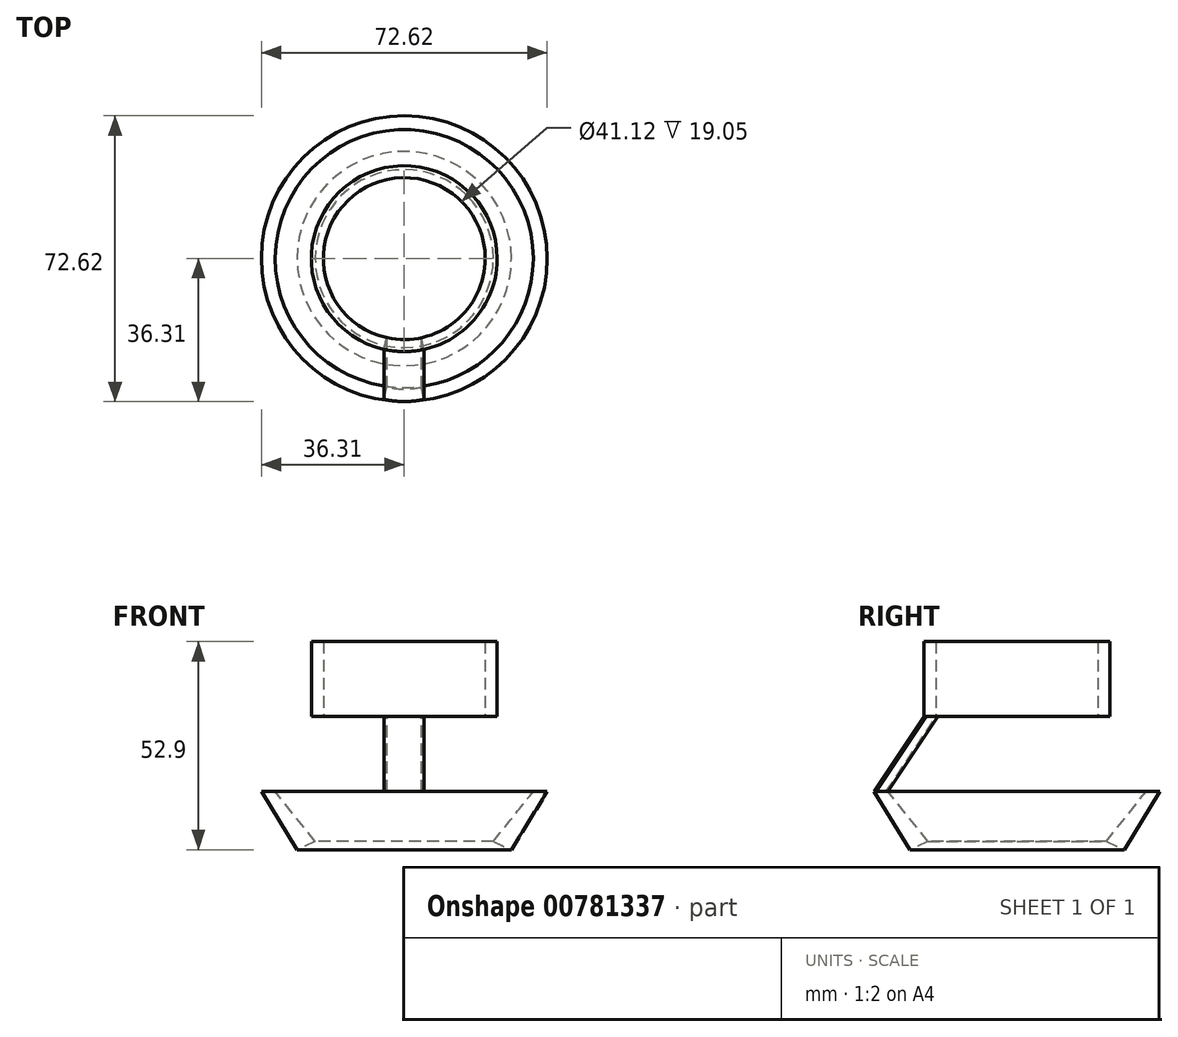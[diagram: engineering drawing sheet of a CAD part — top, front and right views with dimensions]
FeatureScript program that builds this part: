
annotation { "Feature Type Name" : "Feature", "Feature Type Description" : "" }
export const myFeature = defineFeature(function(context is Context, id is Id, definition is map)
    precondition{}
    {
        {
            var Q0;
            Q0=qCreatedBy(makeId("Top.planeOp"),FACE);
            var sketch = newSketch(context, id + "F0", { "sketchPlane" : qUnion([Q0])});
            skCircle(sketch, "E0", {"center": v(0, 0) * mm, "radius": 20.56 * mm});
            skCircle(sketch, "E1.0", {"center": v(0, 0) * mm, "radius": 23.6 * mm});
            skSolve(sketch);
        }
        {
            var Q0;
            Q0 = qSketchRegion(id + "F0", true);
            extrude(context, id + "F1", {"entities" : qUnion([Q0]), "depth" : 19.05 * mm, "offsetDistance" : 25.4 * mm});
        }
        {
            var Q0;
            Q0=makeQuery(id+"F1.opExtrude","CAP_FACE",FACE,{"disambiguationData":[OSD([sQuery(id+"F0.wireOp",EDGE,"E0"),sQuery(id+"F0.wireOp",EDGE,"E1.0")])],"isStart":true});
            var sketch = newSketch(context, id + "F2", { "sketchPlane" : qUnion([Q0])});
            skLineSegment(sketch, "E2", {"start": v(0, 0) * mm, "end": v(0, 22.55) * mm, "construction": true});
            skLineSegment(sketch, "E3", {"start": v(0, 22.55) * mm, "end": v(5.08, 22.55) * mm, "construction": true});
            skLineSegment(sketch, "E4", {"start": v(0, 22.55) * mm, "end": v(-5.08, 22.55) * mm, "construction": true});
            skLineSegment(sketch, "E5", {"start": v(-5.08, 22.55) * mm, "end": v(-5.08, 19.92) * mm, "construction": true});
            skLineSegment(sketch, "E6", {"start": v(5.08, 22.55) * mm, "end": v(5.08, 19.92) * mm, "construction": true});
            skLineSegment(sketch, "E7", {"start": v(-5.08, 23.06) * mm, "end": v(-4.42, 20.08) * mm});
            skLineSegment(sketch, "E8", {"start": v(5.08, 23.06) * mm, "end": v(4.42, 20.08) * mm});
            skArc(sketch, "E9.0", {"start": v(5.08, 23.06) * mm, "mid": v(0, 23.6) * mm, "end": v(-5.08, 23.06) * mm});
            skArc(sketch, "E10.0", {"start": v(5.08, 19.92) * mm, "mid": v(0, 20.56) * mm, "end": v(-5.08, 19.92) * mm});
            skPoint(sketch, "E11", {"position": v(-19.8, 0) * mm});
            skPoint(sketch, "E12", {"position": v(0, 23.6) * mm});
            skSolve(sketch);
        }
        {
            var Q0;
            Q0=qCreatedBy(makeId("Right.planeOp"),FACE);
            var sketch = newSketch(context, id + "F3", { "sketchPlane" : qUnion([Q0])});
            skPoint(sketch, "E13.0", {"position": v(-23.6, 0) * mm});
            skLineSegment(sketch, "E14", {"start": v(-23.6, 0) * mm, "end": v(-36.3, 0) * mm, "construction": true});
            skLineSegment(sketch, "E15", {"start": v(-36.3, 0) * mm, "end": v(-36.3, -19.05) * mm, "construction": true});
            skLineSegment(sketch, "E16", {"start": v(-36.3, -19.05) * mm, "end": v(-23.6, 0) * mm});
            skSolve(sketch);
        }
        {
            var Q0;
            {var subQ0=sQuery(id+"F2.wireOp",EDGE,"E7");Q0=makeQuery(id+"F2.imprint","IMPRINT",FACE,{"disambiguationData":[TD([[makeQuery(id+"F2.imprint","IMPRINT",EDGE,{"derivedFrom":subQ0}),1.0]])]});}
            var Q1;
            Q1=sQuery(id+"F3.wireOp",EDGE,"E16");
            sweep(context, id + "F4", {"operationType" : NewBodyOperationType.ADD, "profiles" : qUnion([Q0]), "path" : qUnion([Q1])});
        }
        {
            var Q0;
            Q0=qCreatedBy(makeId("Right.planeOp"),FACE);
            var sketch = newSketch(context, id + "F5", { "sketchPlane" : qUnion([Q0])});
            skLineSegment(sketch, "E17", {"start": v(0, -13.55) * mm, "end": v(0, 29.8) * mm});
            skSolve(sketch);
        }
        {
            var Q0;
            Q0=makeQuery(id+"F4.opSweep","CAP_FACE",FACE,{"disambiguationData":[OSD([sQuery(id+"F2.wireOp",EDGE,"E7"),sQuery(id+"F2.wireOp",EDGE,"E8"),sQuery(id+"F2.wireOp",EDGE,"E9.0"),sQuery(id+"F2.wireOp",EDGE,"E10.0"),sQuery(id+"F3.wireOp",VERTEX,"E16.start")])],"isStart":false});
            var sketch = newSketch(context, id + "F6", { "sketchPlane" : qUnion([Q0])});
            skPoint(sketch, "E18", {"position": v(5.08, 35.76) * mm});
            skPoint(sketch, "E19", {"position": v(4.42, 32.78) * mm});
            skSolve(sketch);
        }
        {
            var Q0;
            Q0=qCreatedBy(makeId("Right.planeOp"),FACE);
            var sketch = newSketch(context, id + "F7", { "sketchPlane" : qUnion([Q0])});
            skPoint(sketch, "E20.0", {"position": v(-35.76, -19.05) * mm});
            skPoint(sketch, "E21.0", {"position": v(-32.78, -19.05) * mm});
            skLineSegment(sketch, "E22", {"start": v(-32.78, -19.05) * mm, "end": v(-22.62, -19.05) * mm, "construction": true});
            skLineSegment(sketch, "E23", {"start": v(-22.62, -19.05) * mm, "end": v(-22.62, -31.75) * mm, "construction": true});
            skLineSegment(sketch, "E24", {"start": v(-32.78, -19.05) * mm, "end": v(-22.62, -31.75) * mm});
            skLineSegment(sketch, "E25", {"start": v(0, 0) * mm, "end": v(0, -32.23) * mm});
            skPoint(sketch, "E26.0", {"position": v(-36.3, -19.05) * mm});
            skLineSegment(sketch, "E27", {"start": v(-36.3, -19.05) * mm, "end": v(-27.23, -33.85) * mm});
            skLineSegment(sketch, "E28", {"start": v(-27.23, -33.85) * mm, "end": v(-22.62, -31.75) * mm});
            skLineSegment(sketch, "E29", {"start": v(-36.3, -19.05) * mm, "end": v(-32.78, -19.05) * mm});
            skSolve(sketch);
        }
        {
            var Q0;
            Q0 = qSketchRegion(id + "F7", true);
            var Q1;
            Q1=sQuery(id+"F7.wireOp",EDGE,"E25");
            revolve(context, id + "F8", {"operationType" : NewBodyOperationType.ADD, "surfaceOperationType" : NewSurfaceOperationType.NEW, "entities" : qUnion([Q0]), "axis" : qUnion([Q1]), "revolveType" : RevolveType.FULL});
        }
    });
